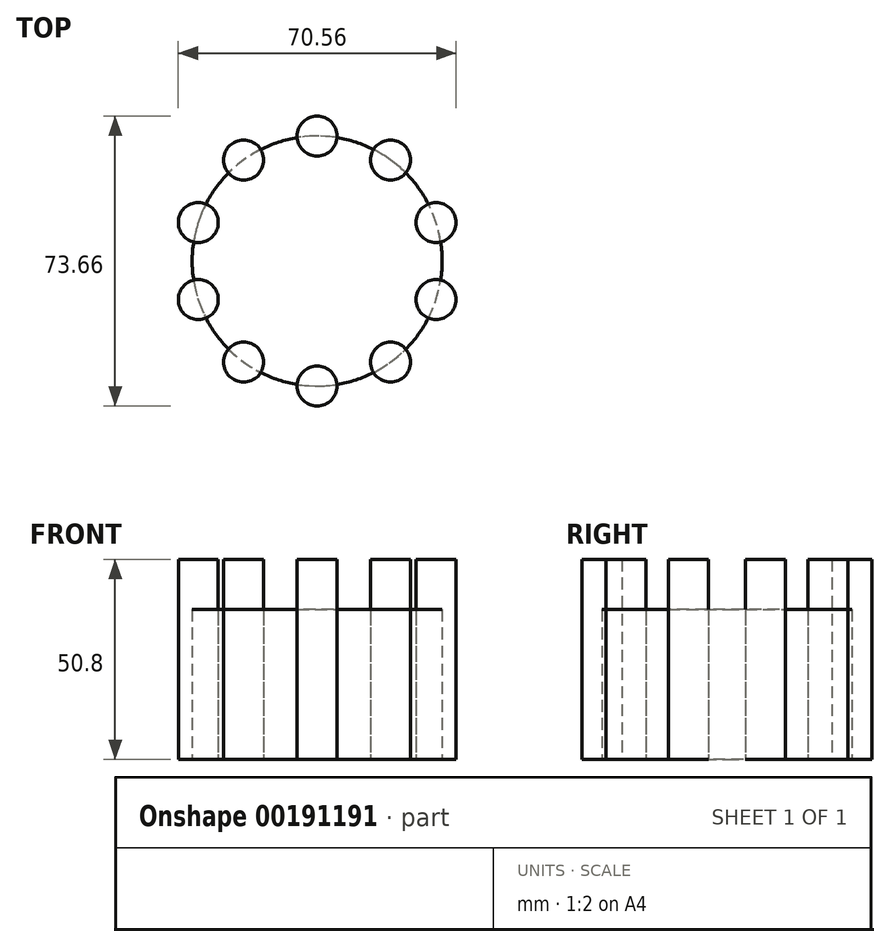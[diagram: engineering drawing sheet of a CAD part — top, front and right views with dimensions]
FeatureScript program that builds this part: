
annotation { "Feature Type Name" : "Feature", "Feature Type Description" : "" }
export const myFeature = defineFeature(function(context is Context, id is Id, definition is map)
    precondition{}
    {
        {
            var Q0;
            Q0=qCreatedBy(makeId("Top.planeOp"),FACE);
            var sketch = newSketch(context, id + "F0", { "sketchPlane" : qUnion([Q0])});
            skCircle(sketch, "E0", {"center": v(0, 0) * mm, "radius": 31.75 * mm});
            skSolve(sketch);
        }
        {
            var Q0;
            Q0=makeQuery(id+"F0.imprint","IMPRINT",FACE,{"disambiguationData":[TD([[makeQuery(id+"F0.imprint","IMPRINT",EDGE,{"derivedFrom":sQuery(id+"F0.wireOp",EDGE,"E0")}),1.0]])]});
            extrude(context, id + "F1", {"entities" : qUnion([Q0]), "depth" : 38.1 * mm});
        }
        {
            var Q0;
            Q0=qCreatedBy(makeId("Top.planeOp"),FACE);
            var sketch = newSketch(context, id + "F2", { "sketchPlane" : qUnion([Q0])});
            skCircle(sketch, "E1", {"center": v(0, 31.75) * mm, "radius": 5.08 * mm});
            skCircle(sketch, "E2.1.0", {"center": v(-18.66, 25.69) * mm, "radius": 5.08 * mm});
            skCircle(sketch, "E2.2.0", {"center": v(-30.2, 9.81) * mm, "radius": 5.08 * mm});
            skCircle(sketch, "E2.3.0", {"center": v(-30.2, -9.81) * mm, "radius": 5.08 * mm});
            skCircle(sketch, "E2.4.0", {"center": v(-18.66, -25.69) * mm, "radius": 5.08 * mm});
            skCircle(sketch, "E2.5.0", {"center": v(0, -31.75) * mm, "radius": 5.08 * mm});
            skCircle(sketch, "E2.6.0", {"center": v(18.66, -25.69) * mm, "radius": 5.08 * mm});
            skCircle(sketch, "E2.7.0", {"center": v(30.2, -9.81) * mm, "radius": 5.08 * mm});
            skCircle(sketch, "E2.8.0", {"center": v(30.2, 9.81) * mm, "radius": 5.08 * mm});
            skCircle(sketch, "E2.9.0", {"center": v(18.66, 25.69) * mm, "radius": 5.08 * mm});
            skPoint(sketch, "E2.center", {"position": v(0, 0) * mm});
            skSolve(sketch);
        }
        {
            var Q0;
            Q0 = qSketchRegion(id + "F2", true);
            extrude(context, id + "F3", {"entities" : qUnion([Q0]), "depth" : 50.8 * mm});
        }
    });
